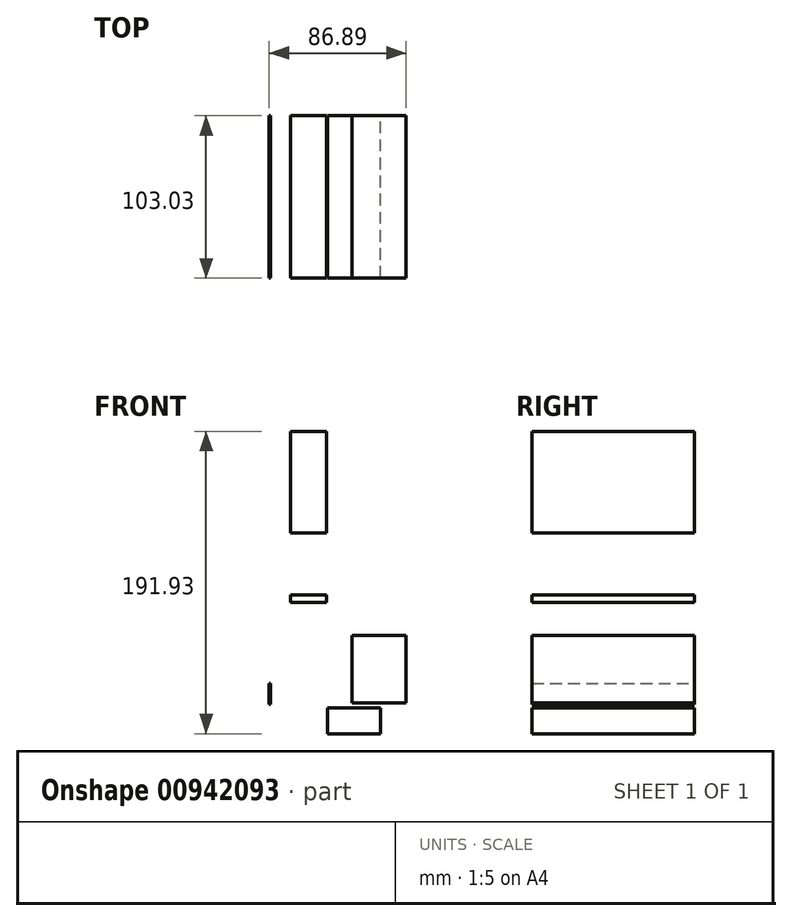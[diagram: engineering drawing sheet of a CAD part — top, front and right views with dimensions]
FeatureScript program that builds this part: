
annotation { "Feature Type Name" : "Feature", "Feature Type Description" : "" }
export const myFeature = defineFeature(function(context is Context, id is Id, definition is map)
    precondition{}
    {
        {
            var Q0;
            Q0=qCreatedBy(makeId("Front.planeOp"),FACE);
            var sketch = newSketch(context, id + "F0", { "sketchPlane" : qUnion([Q0])});
            skLineSegment(sketch, "E0.bottom", {"start": v(-7.3, 25.81) * mm, "end": v(15.63, 25.81) * mm});
            skLineSegment(sketch, "E0.top", {"start": v(-7.3, 20.76) * mm, "end": v(15.63, 20.76) * mm});
            skLineSegment(sketch, "E0.left", {"start": v(-7.3, 25.81) * mm, "end": v(-7.3, 20.76) * mm});
            skLineSegment(sketch, "E0.right", {"start": v(15.63, 25.81) * mm, "end": v(15.63, 20.76) * mm});
            skLineSegment(sketch, "E1.bottom", {"start": v(31.67, 0) * mm, "end": v(66.05, 0) * mm});
            skLineSegment(sketch, "E1.top", {"start": v(31.67, -43.02) * mm, "end": v(66.05, -43.02) * mm});
            skLineSegment(sketch, "E1.left", {"start": v(31.67, 0) * mm, "end": v(31.67, -43.02) * mm});
            skLineSegment(sketch, "E1.right", {"start": v(66.05, 0) * mm, "end": v(66.05, -43.02) * mm});
            skLineSegment(sketch, "E2.bottom", {"start": v(-20, -30.57) * mm, "end": v(-20.84, -30.57) * mm});
            skLineSegment(sketch, "E2.top", {"start": v(-20, -43.73) * mm, "end": v(-20.84, -43.73) * mm});
            skLineSegment(sketch, "E2.left", {"start": v(-20, -30.57) * mm, "end": v(-20, -43.73) * mm});
            skLineSegment(sketch, "E2.right", {"start": v(-20.84, -30.57) * mm, "end": v(-20.84, -43.73) * mm});
            skLineSegment(sketch, "E3.bottom", {"start": v(16.04, -46.2) * mm, "end": v(50, -46.2) * mm});
            skLineSegment(sketch, "E3.top", {"start": v(16.04, -62.45) * mm, "end": v(50, -62.45) * mm});
            skLineSegment(sketch, "E3.left", {"start": v(16.04, -46.2) * mm, "end": v(16.04, -62.45) * mm});
            skLineSegment(sketch, "E3.right", {"start": v(50, -46.2) * mm, "end": v(50, -62.45) * mm});
            skLineSegment(sketch, "E4.bottom", {"start": v(-7.3, 129.48) * mm, "end": v(15.63, 129.48) * mm});
            skLineSegment(sketch, "E4.top", {"start": v(-7.3, 65.18) * mm, "end": v(15.63, 65.18) * mm});
            skLineSegment(sketch, "E4.left", {"start": v(-7.3, 129.48) * mm, "end": v(-7.3, 65.18) * mm});
            skLineSegment(sketch, "E4.right", {"start": v(15.63, 129.48) * mm, "end": v(15.63, 65.18) * mm});
            skSolve(sketch);
        }
        {
            var Q0;
            Q0 = qSketchRegion(id + "F0", true);
            extrude(context, id + "F1", {"entities" : qUnion([Q0]), "depth" : 103.03 * mm, "offsetDistance" : 25.4 * mm});
        }
    });
